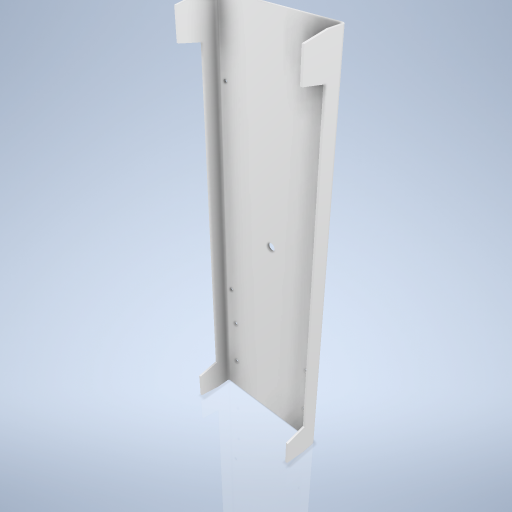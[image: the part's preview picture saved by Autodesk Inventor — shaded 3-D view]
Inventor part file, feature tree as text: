
AUTODESK INVENTOR PART (.ipt)
format: ipt  version: 2024.2 (Build 282272000, 272)  size: 365,056 bytes
history: native  units: mm
features: sketch x8, other x6, hole x5, extrude x1, plane x1, mirror x1, projected_geometry x1
ambient origin geometry x8: Origin, YZ Plane, XZ Plane, XY Plane, X Axis, Y Axis, Z Axis, Center Point
bodies: Volumenkörper1 (feature_tree)
feature tree (23):
  other  "Fläche3"
  other  "Lasche1"
  extrude  "Extrusion2"  Depth=280.0mm
  plane  "Arbeitsebene1"
  mirror  "Spiegeln1"
  hole  "Bohrung1"  [1 undecoded]
  hole  "Bohrung2"  [1 undecoded]
  sketch  "Skizze6"  dims[d12=5.0mm d15=10.0mm]
  hole  "Bohrung3"  [1 undecoded]
  hole  "Bohrung5"  [1 undecoded]
  hole  "Bohrung6"  [1 undecoded]
  sketch  "Skizze1"  dims[d0=950.0mm d1=280.0mm]
  sketch  "Skizze2"  dims[d2=5.0mm d3=5.0mm]
  other  "Grobblech2"
  other  "Biegung1"
  other  "Ecke1"
  sketch  "Skizze3"  dims[d4=2.5mm d5=10.0mm]
  sketch  "Skizze4"  dims[d6=5.0mm d7=96.0mm d8=90.0deg d9=5.0mm]
  sketch  "Skizze5"  dims[d10=20.0mm d11=5.0mm]
  sketch  "Skizze7"  dims[d16=64.0mm]
  other  "Grobblech4"
  projected_geometry  "Projizierte Kontur1"
  sketch  "Skizze8"  dims[d17=10.0mm d18=10.0mm d19=64.0mm d22=54.048mm d25=0.0mm d26=12.0mm d27=6.0mm d28=4.0mm d29=2.0mm d30=90.0deg d31=5.0mm d32=0.0mm d34=220.0mm d36=12.0mm d37=6.0mm d38=4.0mm d39=2.0mm d40=90.0deg d41=8.0mm d42=0.0mm d43=120.0mm d46=10.106mm d47=24.0mm d48=4.0mm d49=2.0mm d50=90.0deg d51=8.0mm d52=0.0mm d55=245.0mm d63=8.376mm d64=107.0mm d65=4.0mm d66=2.0mm d67=90.0deg d68=8.0mm d69=0.0mm d72=107.0mm d73=255.0mm d74=10.0mm d75=0.0mm d76=84.0mm d77=110.0mm d79=14.0mm d80=314.0mm d81=20.0mm d82=107.0mm d83=4.0mm d84=2.0mm d85=90.0deg d86=8.0mm d87=0.0mm d88=122.5mm d89=95.0mm]
note: 5 required parameter values undecoded (feature->parameter linkage not recoverable at this tier; creation-order binding heuristic only, values carry confidence <= 0.55)
